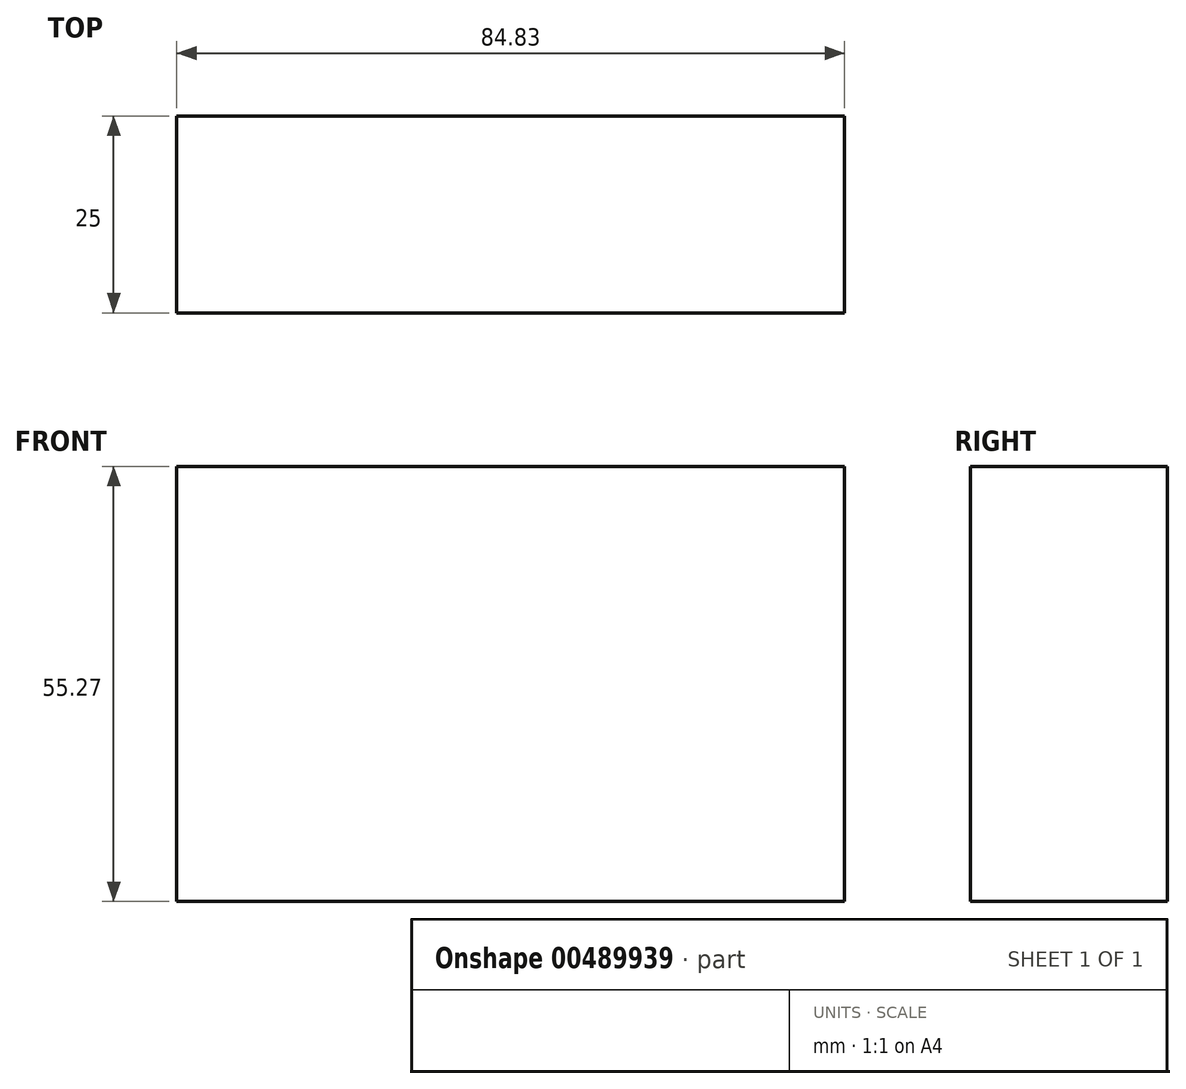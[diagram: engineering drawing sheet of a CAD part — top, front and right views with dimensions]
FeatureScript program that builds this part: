
annotation { "Feature Type Name" : "Feature", "Feature Type Description" : "" }
export const myFeature = defineFeature(function(context is Context, id is Id, definition is map)
    precondition{}
    {
        {
            var Q0;
            Q0=qCreatedBy(makeId("Front.planeOp"),FACE);
            var sketch = newSketch(context, id + "F0", { "sketchPlane" : qUnion([Q0])});
            skLineSegment(sketch, "E0.bottom", {"start": v(-41.77, 22.5) * mm, "end": v(43.06, 22.5) * mm});
            skLineSegment(sketch, "E0.top", {"start": v(-41.77, -32.78) * mm, "end": v(43.06, -32.78) * mm});
            skLineSegment(sketch, "E0.left", {"start": v(-41.77, 22.5) * mm, "end": v(-41.77, -32.78) * mm});
            skLineSegment(sketch, "E0.right", {"start": v(43.06, 22.5) * mm, "end": v(43.06, -32.78) * mm});
            skSolve(sketch);
        }
        {
            var Q0;
            Q0 = qSketchRegion(id + "F0", true);
            extrude(context, id + "F1", {"entities" : qUnion([Q0]), "depth" : 25 * mm});
        }
    });
